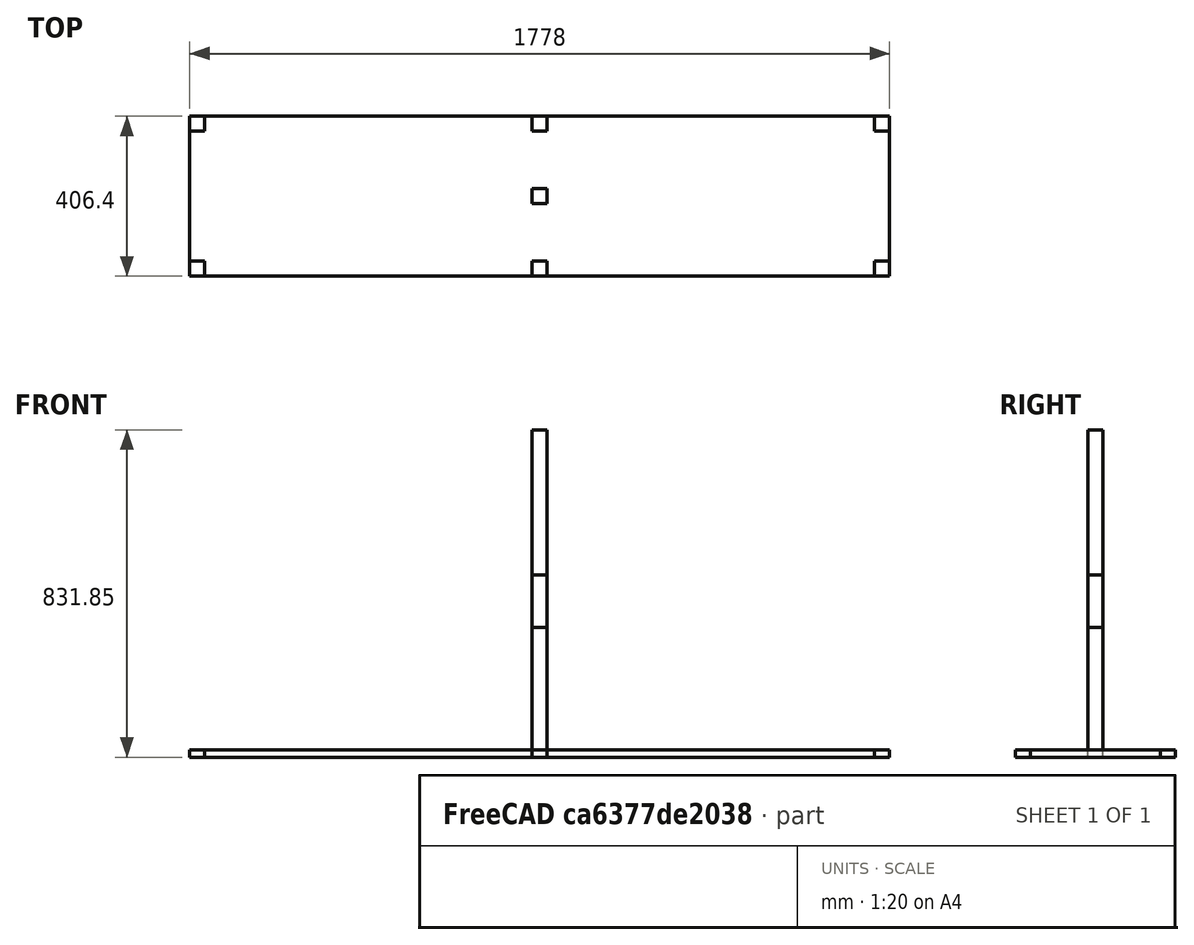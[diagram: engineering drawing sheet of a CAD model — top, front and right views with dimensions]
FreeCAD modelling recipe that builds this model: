
FCSTD DOCUMENT  (FreeCAD 1.1R41155 (Git))
Label: tv_console
License: All rights reserved
LicenseURL: http://en.wikipedia.org/wiki/All_rights_reserved
objects: App::FeaturePython×25, App::Link×22, App::Point×7, Sketcher::SketchObject×5, PartDesign::Pad×5, PartDesign::Body×5, Spreadsheet::Sheet×1, Assembly::JointGroup×1, Assembly::ViewGroup×1, Assembly::BomObject×1, Assembly::BomGroup×1, Assembly::AssemblyObject×1
note: 30 computed .brp shape members not serialized (recipe doc carries the construction recipe); baked Part::Feature solids carry a one-line shape summary decoded from their .brp

FEATURE [Sketcher::SketchObject] Sketch
  ArcFitTolerance = 0
  AttachmentSupport = -> [XY_Plane]
  ExternalTypes = [0]
  FullyConstrained = true
  MakeInternals = false
  MapMode = 5
  sketch-geometry (5):
    g0: LineSegment StartX=-889 StartY=-203.2 StartZ=0 EndX=889 EndY=-203.2 EndZ=0
    g1: LineSegment StartX=889 StartY=-203.2 StartZ=0 EndX=889 EndY=203.2 EndZ=0
    g2: LineSegment StartX=889 StartY=203.2 StartZ=0 EndX=-889 EndY=203.2 EndZ=0
    g3: LineSegment StartX=-889 StartY=203.2 StartZ=0 EndX=-889 EndY=-203.2 EndZ=0
    g4: GeomPoint [constr] X=0 Y=0 Z=0
  constraints (12):
    c: Coincident(g0,g1)
    c: Coincident(g1,g2)
    c: Coincident(g2,g3)
    c: Coincident(g3,g0)
    c: Horizontal(g0)
    c: Horizontal(g2)
    c: Vertical(g1)
    c: Vertical(g3)
    c: Symmetric(g2,g0,g4)
    c: Distance(g1,g3) = 1778
    c: Distance(g0,g2) = 406.4
    c: Coincident(g4,g-1)
FEATURE [PartDesign::Pad] Pad
  Direction = (0,0,1)
  Length = 19.05
  Length2 = 10
  Profile = -> Sketch
  ReferenceAxis = -> Sketch [N_Axis]
  Suppressed = false
  Type = 0
  expr: Length = Spreadsheet.plywood_thickness
FEATURE [PartDesign::Body] Body  label="top"
  AllowCompound = false
  Group = -> [Sketch,Pad]
  Origin = -> Origin
  Tip = -> Pad
FEATURE [Sketcher::SketchObject] Sketch001
  ArcFitTolerance = 0
  AttachmentSupport = -> [XY_Plane001]
  ExternalTypes = [0]
  FullyConstrained = true
  MakeInternals = false
  MapMode = 5
  sketch-geometry (5):
    g0: LineSegment StartX=-19.05 StartY=-19.05 StartZ=0 EndX=19.05 EndY=-19.05 EndZ=0
    g1: LineSegment StartX=19.05 StartY=-19.05 StartZ=0 EndX=19.05 EndY=19.05 EndZ=0
    g2: LineSegment StartX=19.05 StartY=19.05 StartZ=0 EndX=-19.05 EndY=19.05 EndZ=0
    g3: LineSegment StartX=-19.05 StartY=19.05 StartZ=0 EndX=-19.05 EndY=-19.05 EndZ=0
    g4: GeomPoint [constr] X=0 Y=0 Z=0
  constraints (12):
    c: Coincident(g0,g1)
    c: Coincident(g1,g2)
    c: Coincident(g2,g3)
    c: Coincident(g3,g0)
    c: Horizontal(g0)
    c: Horizontal(g2)
    c: Vertical(g1)
    c: Vertical(g3)
    c: Symmetric(g2,g0,g4)
    c: Distance(g1,g3) = 38.1
    c: Distance(g0,g2) = 38.1
    c: Coincident(g4,g-1)
FEATURE [Spreadsheet::Sheet] Spreadsheet
  cells = B3='plywood thickness; C3(plywood_thickness)==0.75 "
FEATURE [PartDesign::Pad] Pad001
  Direction = (0,0,1)
  Length = 463.55
  Length2 = 10
  Profile = -> Sketch001
  ReferenceAxis = -> Sketch001 [N_Axis]
  Suppressed = false
  Type = 0
  expr: Length = 19 " - Spreadsheet.plywood_thickness
FEATURE [PartDesign::Body] Body001  label="leg"
  AllowCompound = false
  Group = -> [Sketch001,Pad001]
  Origin = -> Origin001
  Tip = -> Pad001
FEATURE [Sketcher::SketchObject] Sketch002
  ArcFitTolerance = 0
  AttachmentSupport = -> [XY_Plane002]
  ExternalTypes = [0]
  FullyConstrained = false
  MakeInternals = false
  MapMode = 5
  sketch-geometry (24):
    g0: LineSegment StartX=0 StartY=165.1 StartZ=0 EndX=19.05 EndY=165.1 EndZ=0
    g1: LineSegment StartX=19.05 StartY=165.1 StartZ=0 EndX=19.05 EndY=203.2 EndZ=0
    g2: LineSegment StartX=19.05 StartY=203.2 StartZ=0 EndX=850.9 EndY=203.2 EndZ=0
    g3: LineSegment StartX=850.9 StartY=203.2 StartZ=0 EndX=850.9 EndY=165.1 EndZ=0
    g4: LineSegment StartX=850.9 StartY=165.1 StartZ=0 EndX=889 EndY=165.1 EndZ=0
    g5: LineSegment StartX=889 StartY=165.1 StartZ=0 EndX=889 EndY=0 EndZ=0
    g6: LineSegment StartX=0 StartY=-165.1 StartZ=0 EndX=19.05 EndY=-165.1 EndZ=0
    g7: LineSegment StartX=19.05 StartY=-165.1 StartZ=0 EndX=19.05 EndY=-203.2 EndZ=0
    g8: LineSegment StartX=19.05 StartY=-203.2 StartZ=0 EndX=850.9 EndY=-203.2 EndZ=0
    g9: LineSegment StartX=850.9 StartY=-203.2 StartZ=0 EndX=850.9 EndY=-165.1 EndZ=0
    g10: LineSegment StartX=850.9 StartY=-165.1 StartZ=0 EndX=889 EndY=-165.1 EndZ=0
    g11: LineSegment StartX=889 StartY=-165.1 StartZ=0 EndX=889 EndY=0 EndZ=0
    g12: LineSegment StartX=0 StartY=165.1 StartZ=0 EndX=-19.05 EndY=165.1 EndZ=0
    g13: LineSegment StartX=-19.05 StartY=165.1 StartZ=0 EndX=-19.05 EndY=203.2 EndZ=0
    g14: LineSegment StartX=-19.05 StartY=203.2 StartZ=0 EndX=-850.9 EndY=203.2 EndZ=0
    g15: LineSegment StartX=-850.9 StartY=203.2 StartZ=0 EndX=-850.9 EndY=165.1 EndZ=0
    g16: LineSegment StartX=-850.9 StartY=165.1 StartZ=0 EndX=-889 EndY=165.1 EndZ=0
    g17: LineSegment StartX=-889 StartY=165.1 StartZ=0 EndX=-889 EndY=0 EndZ=0
    g18: LineSegment StartX=0 StartY=-165.1 StartZ=0 EndX=-19.05 EndY=-165.1 EndZ=0
    g19: LineSegment StartX=-19.05 StartY=-165.1 StartZ=0 EndX=-19.05 EndY=-203.2 EndZ=0
    g20: LineSegment StartX=-19.05 StartY=-203.2 StartZ=0 EndX=-850.9 EndY=-203.2 EndZ=0
    g21: LineSegment StartX=-850.9 StartY=-203.2 StartZ=0 EndX=-850.9 EndY=-165.1 EndZ=0
    g22: LineSegment StartX=-850.9 StartY=-165.1 StartZ=0 EndX=-889 EndY=-165.1 EndZ=0
    g23: LineSegment StartX=-889 StartY=-165.1 StartZ=0 EndX=-889 EndY=0 EndZ=0
  constraints (58):
    c: PointOnObject(g0,g-2)
    c: Horizontal(g0)
    c: Coincident(g0,g1)
    c: Vertical(g1)
    c: Coincident(g1,g2)
    c: Horizontal(g2)
    c: Coincident(g2,g3)
    c: Vertical(g3)
    c: Coincident(g3,g4)
    c: Horizontal(g4)
    c: Coincident(g4,g5)
    c: PointOnObject(g5,g-1)
    c: Vertical(g5)
    c: DistanceY(g1,g1) = 38.1
    c: DistanceX(g0,g0) = 19.05
    c: Equal(g3,g1)
    c: DistanceY(g5,g2) = 203.2
    c: DistanceX(g0,g4) = 889
    c: Equal(g4,g3)
    c: Horizontal(g6)
    c: Coincident(g6,g7)
    c: Vertical(g7)
    c: Coincident(g7,g8)
    c: Horizontal(g8)
    c: Coincident(g8,g9)
    c: Vertical(g9)
    c: Coincident(g9,g10)
    c: Horizontal(g10)
    c: Coincident(g10,g11)
    c: Vertical(g11)
    c: Equal(g9,g7)
    c: Equal(g10,g9)
    c: Horizontal(g12)
    c: Coincident(g12,g13)
    c: Vertical(g13)
    c: Coincident(g13,g14)
    c: Horizontal(g14)
    c: Coincident(g14,g15)
    c: Vertical(g15)
    c: Coincident(g15,g16)
    c: Horizontal(g16)
    c: Coincident(g16,g17)
    c: Vertical(g17)
    c: Equal(g15,g13)
    c: Equal(g16,g15)
    c: Horizontal(g18)
    c: Coincident(g18,g19)
    c: Vertical(g19)
    c: Coincident(g19,g20)
    c: Horizontal(g20)
    c: Coincident(g20,g21)
    c: Vertical(g21)
    c: Coincident(g21,g22)
    c: Horizontal(g22)
    c: Coincident(g22,g23)
    c: Vertical(g23)
    c: Equal(g21,g19)
    c: Equal(g22,g21)
FEATURE [PartDesign::Pad] Pad002
  Direction = (0,0,1)
  Length = 19.05
  Length2 = 10
  Profile = -> Sketch002
  ReferenceAxis = -> Sketch002 [N_Axis]
  Suppressed = false
  Type = 0
  expr: Length = Spreadsheet.plywood_thickness
FEATURE [PartDesign::Body] Body002  label="shelf"
  AllowCompound = false
  Group = -> [Sketch002,Pad002]
  Origin = -> Origin002
  Tip = -> Pad002
FEATURE [Sketcher::SketchObject] Sketch003
  ArcFitTolerance = 0
  AttachmentSupport = -> [XY_Plane004]
  ExternalTypes = [0]
  FullyConstrained = true
  MakeInternals = false
  MapMode = 5
  sketch-geometry (5):
    g0: LineSegment StartX=-19.05 StartY=-19.05 StartZ=0 EndX=19.05 EndY=-19.05 EndZ=0
    g1: LineSegment StartX=19.05 StartY=-19.05 StartZ=0 EndX=19.05 EndY=19.05 EndZ=0
    g2: LineSegment StartX=19.05 StartY=19.05 StartZ=0 EndX=-19.05 EndY=19.05 EndZ=0
    g3: LineSegment StartX=-19.05 StartY=19.05 StartZ=0 EndX=-19.05 EndY=-19.05 EndZ=0
    g4: GeomPoint [constr] X=0 Y=0 Z=0
  constraints (12):
    c: Coincident(g0,g1)
    c: Coincident(g1,g2)
    c: Coincident(g2,g3)
    c: Coincident(g3,g0)
    c: Horizontal(g0)
    c: Horizontal(g2)
    c: Vertical(g1)
    c: Vertical(g3)
    c: Symmetric(g2,g0,g4)
    c: Distance(g1,g3) = 38.1
    c: Distance(g0,g2) = 38.1
    c: Coincident(g4,g-1)
FEATURE [PartDesign::Pad] Pad003
  Direction = (0,0,1)
  Length = 831.85
  Length2 = 10
  Profile = -> Sketch003
  ReferenceAxis = -> Sketch003 [N_Axis]
  Suppressed = false
  Type = 0
  expr: Length = 35 " - 2.25 "
FEATURE [PartDesign::Body] Body004  label="long support"
  AllowCompound = false
  Group = -> [Sketch003,Pad003]
  Origin = -> Origin004
  Tip = -> Pad003
FEATURE [Sketcher::SketchObject] Sketch004
  ArcFitTolerance = 0
  AttachmentSupport = -> [XY_Plane005]
  ExternalTypes = [0]
  FullyConstrained = true
  MakeInternals = false
  MapMode = 5
  sketch-geometry (5):
    g0: LineSegment StartX=-19.05 StartY=-19.05 StartZ=0 EndX=19.05 EndY=-19.05 EndZ=0
    g1: LineSegment StartX=19.05 StartY=-19.05 StartZ=0 EndX=19.05 EndY=19.05 EndZ=0
    g2: LineSegment StartX=19.05 StartY=19.05 StartZ=0 EndX=-19.05 EndY=19.05 EndZ=0
    g3: LineSegment StartX=-19.05 StartY=19.05 StartZ=0 EndX=-19.05 EndY=-19.05 EndZ=0
    g4: GeomPoint [constr] X=0 Y=0 Z=0
  constraints (12):
    c: Coincident(g0,g1)
    c: Coincident(g1,g2)
    c: Coincident(g2,g3)
    c: Coincident(g3,g0)
    c: Horizontal(g0)
    c: Horizontal(g2)
    c: Vertical(g1)
    c: Vertical(g3)
    c: Symmetric(g2,g0,g4)
    c: Distance(g1,g3) = 38.1
    c: Distance(g0,g2) = 38.1
    c: Coincident(g4,g-1)
FEATURE [PartDesign::Pad] Pad004
  Direction = (0,0,1)
  Length = 330.2
  Length2 = 10
  Profile = -> Sketch004
  ReferenceAxis = -> Sketch004 [N_Axis]
  Suppressed = false
  Type = 0
  expr: Length = 13 "
FEATURE [PartDesign::Body] Body005  label="short support"
  AllowCompound = false
  Group = -> [Sketch004,Pad004]
  Origin = -> Origin005
  Tip = -> Pad004
FEATURE [App::Point] Origin008  label="Origin"
  Role = Origin
FEATURE [App::Point] Origin009  label="Origin"
  Role = Origin
FEATURE [App::Point] Origin010  label="Origin"
  Role = Origin
FEATURE [App::Point] Origin011  label="Origin"
  Role = Origin
FEATURE [App::Point] Origin012  label="Origin"
  Role = Origin
FEATURE [App::Point] Origin013  label="Origin"
  Role = Origin
FEATURE [App::Point] Origin015
  Role = Origin
FEATURE [App::Link] top
  LinkedObject = -> Body
FEATURE [App::FeaturePython] GroundedJoint  # Assembly grounded joint (typed FeaturePython)
  ObjectToGround = -> top
FEATURE [App::Link] shelf
  LinkPlacement = pos=(0,4.3273e-05,-363) rot=(0,0,1;0rad)
  LinkedObject = -> Body002
  Placement = pos=(0,4.3273e-05,-363) rot=(0,0,1;0rad)
FEATURE [App::Link] leg
  LinkPlacement = pos=(869.95,-184.15,-463.55) rot=(0,0,1;0rad)
  LinkedObject = -> Body001
  Placement = pos=(869.95,-184.15,-463.55) rot=(0,0,1;0rad)
FEATURE [App::Link] leg001
  LinkPlacement = pos=(-869.95,-184.15,-463.55) rot=(0,0,1;0rad)
  LinkedObject = -> Body001
  Placement = pos=(-869.95,-184.15,-463.55) rot=(0,0,1;0rad)
FEATURE [App::Link] leg002
  LinkPlacement = pos=(-869.95,184.15,-463.55) rot=(0,0,1;0rad)
  LinkedObject = -> Body001
  Placement = pos=(-869.95,184.15,-463.55) rot=(0,0,1;0rad)
FEATURE [App::Link] leg003
  LinkPlacement = pos=(-2.076e-13,-184.15,-463.55) rot=(0,0,1;0rad)
  LinkedObject = -> Body001
  Placement = pos=(-2.076e-13,-184.15,-463.55) rot=(0,0,1;0rad)
FEATURE [App::Link] leg004
  LinkPlacement = pos=(2.052e-13,184.15,-463.55) rot=(0,0,1;0rad)
  LinkedObject = -> Body001
  Placement = pos=(2.052e-13,184.15,-463.55) rot=(0,0,1;0rad)
FEATURE [App::Link] leg005
  LinkPlacement = pos=(869.95,184.15,-463.55) rot=(0,0,1;0rad)
  LinkedObject = -> Body001
  Placement = pos=(869.95,184.15,-463.55) rot=(0,0,1;0rad)
FEATURE [App::Link] short_support  label="short support001"
  LinkPlacement = pos=(869.95,165.1,-19.05) rot=(1,0,0;1.5708rad)
  LinkedObject = -> Body005
  Placement = pos=(869.95,165.1,-19.05) rot=(1,0,0;1.5708rad)
FEATURE [App::Link] short_support001  label="short support002"
  LinkPlacement = pos=(-869.95,165.1,-19.05) rot=(1,0,0;1.5708rad)
  LinkedObject = -> Body005
  Placement = pos=(-869.95,165.1,-19.05) rot=(1,0,0;1.5708rad)
FEATURE [App::Link] short_support002  label="short support003"
  LinkPlacement = pos=(1.02e-14,165.1,-19.05) rot=(1,0,0;1.5708rad)
  LinkedObject = -> Body005
  Placement = pos=(1.02e-14,165.1,-19.05) rot=(1,0,0;1.5708rad)
FEATURE [App::Link] short_support003  label="short support004"
  LinkPlacement = pos=(0,165.1,-382.05) rot=(1,0,0;1.5708rad)
  LinkedObject = -> Body005
  Placement = pos=(0,165.1,-382.05) rot=(1,0,0;1.5708rad)
FEATURE [App::Link] short_support004  label="short support005"
  LinkPlacement = pos=(869.95,165.1,-382.05) rot=(1,0,0;1.5708rad)
  LinkedObject = -> Body005
  Placement = pos=(869.95,165.1,-382.05) rot=(1,0,0;1.5708rad)
FEATURE [App::Link] short_support005  label="short support006"
  LinkPlacement = pos=(-869.95,165.1,-382.05) rot=(1,0,0;1.5708rad)
  LinkedObject = -> Body005
  Placement = pos=(-869.95,165.1,-382.05) rot=(1,0,0;1.5708rad)
FEATURE [App::Link] long_support  label="long support001"
  LinkPlacement = pos=(19.05,184.15,-19.05) rot=(0,1,0;1.5708rad)
  LinkedObject = -> Body004
  Placement = pos=(19.05,184.15,-19.05) rot=(0,1,0;1.5708rad)
FEATURE [App::Link] long_support001  label="long support002"
  LinkPlacement = pos=(-850.9,184.15,-19.05) rot=(0,1,0;1.5708rad)
  LinkedObject = -> Body004
  Placement = pos=(-850.9,184.15,-19.05) rot=(0,1,0;1.5708rad)
FEATURE [App::Link] long_support002  label="long support003"
  LinkPlacement = pos=(19.05,-184.15,-19.05) rot=(0,1,0;1.5708rad)
  LinkedObject = -> Body004
  Placement = pos=(19.05,-184.15,-19.05) rot=(0,1,0;1.5708rad)
FEATURE [App::Link] long_support003  label="long support004"
  LinkPlacement = pos=(-850.9,-184.15,-19.05) rot=(0,1,0;1.5708rad)
  LinkedObject = -> Body004
  Placement = pos=(-850.9,-184.15,-19.05) rot=(0,1,0;1.5708rad)
FEATURE [App::Link] long_support004  label="long support005"
  LinkPlacement = pos=(-19.05,-184.15,-382.05) rot=(0,1,0;4.71239rad)
  LinkedObject = -> Body004
  Placement = pos=(-19.05,-184.15,-382.05) rot=(0,1,0;4.71239rad)
FEATURE [App::Link] long_support005  label="long support006"
  LinkPlacement = pos=(-19.05,184.15,-382.05) rot=(0,-1,0;1.5708rad)
  LinkedObject = -> Body004
  Placement = pos=(-19.05,184.15,-382.05) rot=(0,-1,0;1.5708rad)
FEATURE [App::Link] long_support006  label="long support007"
  LinkPlacement = pos=(850.9,-184.15,-382.05) rot=(0,-1,0;1.5708rad)
  LinkedObject = -> Body004
  Placement = pos=(850.9,-184.15,-382.05) rot=(0,-1,0;1.5708rad)
FEATURE [App::Link] long_support007  label="long support008"
  LinkPlacement = pos=(850.9,184.15,-382.05) rot=(0,-1,0;1.5708rad)
  LinkedObject = -> Body004
  Placement = pos=(850.9,184.15,-382.05) rot=(0,-1,0;1.5708rad)
FEATURE [App::FeaturePython] Joint  label="Fixed016"  # Assembly joint (typed FeaturePython)
  Activated = true
  AngleMax = 0
  AngleMin = 0
  Detach1 = false
  Detach2 = false
  Distance = 0
  Distance2 = 0
  EnableAngleMax = false
  EnableAngleMin = false
  EnableLengthMax = false
  EnableLengthMin = false
  JointType = 0 (Fixed)
  LengthMax = 0
  LengthMin = 0
  Placement1 = pos=(19.05,-19.05,463.55) rot=(0,0,1;0rad)
  Placement2 = pos=(889,-203.2,0) rot=(0,0,1;0rad)
  Reference1 = -> Assembly [leg.Vertex4,leg.Vertex4]
  Reference2 = -> Assembly [top.Vertex3,top.Vertex3]
FEATURE [App::FeaturePython] Joint001  label="Fixed017"  # Assembly joint (typed FeaturePython)
  Activated = true
  AngleMax = 0
  AngleMin = 0
  Detach1 = false
  Detach2 = false
  Distance = 0
  Distance2 = 0
  EnableAngleMax = false
  EnableAngleMin = false
  EnableLengthMax = false
  EnableLengthMin = false
  JointType = 0 (Fixed)
  LengthMax = 0
  LengthMin = 0
  Placement1 = pos=(0,-203.2,0) rot=(0.707107,0,0.707107;3.14159rad)
  Placement2 = pos=(1.7e-15,-19.05,463.55) rot=(0.707107,0,0.707107;3.14159rad)
  Reference1 = -> Assembly [top.Edge3,top.Edge3]
  Reference2 = -> Assembly [leg003.Edge4,leg003.Edge4]
FEATURE [App::FeaturePython] Joint002  label="Fixed018"  # Assembly joint (typed FeaturePython)
  Activated = true
  AngleMax = 0
  AngleMin = 0
  Detach1 = false
  Detach2 = false
  Distance = 0
  Distance2 = 0
  EnableAngleMax = false
  EnableAngleMin = false
  EnableLengthMax = false
  EnableLengthMin = false
  JointType = 0 (Fixed)
  LengthMax = 0
  LengthMin = 0
  Placement1 = pos=(-889,-203.2,0) rot=(0,0,1;0rad)
  Placement2 = pos=(-19.05,-19.05,463.55) rot=(0,0,1;0rad)
  Reference1 = -> Assembly [top.Vertex1,top.Vertex1]
  Reference2 = -> Assembly [leg001.Vertex2,leg001.Vertex2]
FEATURE [App::FeaturePython] Joint003  label="Fixed019"  # Assembly joint (typed FeaturePython)
  Activated = true
  AngleMax = 0
  AngleMin = 0
  Detach1 = false
  Detach2 = false
  Distance = 0
  Distance2 = 0
  EnableAngleMax = false
  EnableAngleMin = false
  EnableLengthMax = false
  EnableLengthMin = false
  JointType = 0 (Fixed)
  LengthMax = 0
  LengthMin = 0
  Placement1 = pos=(-19.05,19.05,463.55) rot=(0,0,1;0rad)
  Placement2 = pos=(-889,203.2,0) rot=(0,0,1;0rad)
  Reference1 = -> Assembly [leg002.Vertex8,leg002.Vertex8]
  Reference2 = -> Assembly [top.Vertex7,top.Vertex7]
FEATURE [App::FeaturePython] Joint004  label="Fixed020"  # Assembly joint (typed FeaturePython)
  Activated = true
  AngleMax = 0
  AngleMin = 0
  Detach1 = false
  Detach2 = false
  Distance = 0
  Distance2 = 0
  EnableAngleMax = false
  EnableAngleMin = false
  EnableLengthMax = false
  EnableLengthMin = false
  JointType = 0 (Fixed)
  LengthMax = 0
  LengthMin = 0
  Placement1 = pos=(0,203.2,0) rot=(-0.707107,0,0.707107;3.14159rad)
  Placement2 = pos=(7e-16,19.05,463.55) rot=(-0.707107,0,0.707107;3.14159rad)
  Reference1 = -> Assembly [top.Edge9,top.Edge9]
  Reference2 = -> Assembly [leg004.Edge10,leg004.Edge10]
FEATURE [App::FeaturePython] Joint005  label="Fixed021"  # Assembly joint (typed FeaturePython)
  Activated = true
  AngleMax = 0
  AngleMin = 0
  Detach1 = false
  Detach2 = false
  Distance = 0
  Distance2 = 0
  EnableAngleMax = false
  EnableAngleMin = false
  EnableLengthMax = false
  EnableLengthMin = false
  JointType = 0 (Fixed)
  LengthMax = 0
  LengthMin = 0
  Placement1 = pos=(889,203.2,0) rot=(0,0,1;0rad)
  Placement2 = pos=(19.05,19.05,463.55) rot=(0,0,1;0rad)
  Reference1 = -> Assembly [top.Vertex5,top.Vertex5]
  Reference2 = -> Assembly [leg005.Vertex6,leg005.Vertex6]
FEATURE [App::FeaturePython] Joint006  label="Fixed025"  # Assembly joint (typed FeaturePython)
  Activated = true
  AngleMax = 0
  AngleMin = 0
  Detach1 = false
  Detach2 = false
  Distance = 0
  Distance2 = 0
  EnableAngleMax = false
  EnableAngleMin = false
  EnableLengthMax = false
  EnableLengthMin = false
  JointType = 0 (Fixed)
  LengthMax = 0
  LengthMin = 0
  Offset2 = pos=(0,0,0) rot=(0,0,-1;1.5708rad)
  Placement1 = pos=(-19.05,0,0) rot=(-0.57735,-0.57735,0.57735;4.18879rad)
  Placement2 = pos=(19.05,0,463.55) rot=(0,0.707107,0.707107;3.14159rad)
  Reference1 = -> Assembly [long_support001.Edge11,long_support001.Edge11]
  Reference2 = -> Assembly [leg002.Edge7,leg002.Edge7]
FEATURE [App::FeaturePython] Joint007  label="Fixed026"  # Assembly joint (typed FeaturePython)
  Activated = true
  AngleMax = 0
  AngleMin = 0
  Detach1 = false
  Detach2 = false
  Distance = 0
  Distance2 = 0
  EnableAngleMax = false
  EnableAngleMin = false
  EnableLengthMax = false
  EnableLengthMin = false
  JointType = 0 (Fixed)
  LengthMax = 0
  LengthMin = 0
  Offset2 = pos=(0,0,0) rot=(0,0,-1;1.5708rad)
  Placement1 = pos=(-19.05,0,0) rot=(-0.57735,-0.57735,0.57735;4.18879rad)
  Placement2 = pos=(19.05,0,463.55) rot=(0,0.707107,0.707107;3.14159rad)
  Reference1 = -> Assembly [long_support.Edge11,long_support.Edge11]
  Reference2 = -> Assembly [leg004.Edge7,leg004.Edge7]
FEATURE [App::FeaturePython] Joint008  label="Fixed027"  # Assembly joint (typed FeaturePython)
  Activated = true
  AngleMax = 0
  AngleMin = 0
  Detach1 = false
  Detach2 = false
  Distance = 0
  Distance2 = 0
  EnableAngleMax = false
  EnableAngleMin = false
  EnableLengthMax = false
  EnableLengthMin = false
  JointType = 0 (Fixed)
  LengthMax = 0
  LengthMin = 0
  Offset2 = pos=(0,0,0) rot=(0,0,-1;1.5708rad)
  Placement1 = pos=(-19.05,0,831.85) rot=(-0.57735,-0.57735,0.57735;4.18879rad)
  Placement2 = pos=(-19.05,0,463.55) rot=(0,-0.707107,0.707107;3.14159rad)
  Reference1 = -> Assembly [long_support003.Edge12,long_support003.Edge12]
  Reference2 = -> Assembly [leg003.Edge12,leg003.Edge12]
FEATURE [App::FeaturePython] Joint009  label="Fixed028"  # Assembly joint (typed FeaturePython)
  Activated = true
  AngleMax = 0
  AngleMin = 0
  Detach1 = false
  Detach2 = false
  Distance = 0
  Distance2 = 0
  EnableAngleMax = false
  EnableAngleMin = false
  EnableLengthMax = false
  EnableLengthMin = false
  JointType = 0 (Fixed)
  LengthMax = 0
  LengthMin = 0
  Offset2 = pos=(0,0,0) rot=(0,0,1;1.5708rad)
  Placement1 = pos=(-19.05,0,463.55) rot=(-0.57735,-0.57735,0.57735;4.18879rad)
  Placement2 = pos=(-19.05,0,831.85) rot=(-1,0,0;4.71239rad)
  Reference1 = -> Assembly [leg.Edge12,leg.Edge12]
  Reference2 = -> Assembly [long_support002.Edge12,long_support002.Edge12]
FEATURE [App::FeaturePython] Joint010  label="Fixed029"  # Assembly joint (typed FeaturePython)
  Activated = true
  AngleMax = 0
  AngleMin = 0
  Detach1 = false
  Detach2 = false
  Distance = 0
  Distance2 = 0
  EnableAngleMax = false
  EnableAngleMin = false
  EnableLengthMax = false
  EnableLengthMin = false
  JointType = 0 (Fixed)
  LengthMax = 0
  LengthMin = 0
  Offset2 = pos=(0,0,0) rot=(0,0,-1;1.5708rad)
  Placement1 = pos=(0,19.05,0) rot=(-0.707107,0,0.707107;3.14159rad)
  Placement2 = pos=(0,-19.05,463.55) rot=(0.57735,0.57735,0.57735;2.0944rad)
  Reference1 = -> Assembly [short_support.Edge9,short_support.Edge9]
  Reference2 = -> Assembly [leg005.Edge4,leg005.Edge4]
FEATURE [App::FeaturePython] Joint011  label="Fixed030"  # Assembly joint (typed FeaturePython)
  Activated = true
  AngleMax = 0
  AngleMin = 0
  Detach1 = false
  Detach2 = false
  Distance = 0
  Distance2 = 0
  EnableAngleMax = false
  EnableAngleMin = false
  EnableLengthMax = false
  EnableLengthMin = false
  JointType = 0 (Fixed)
  LengthMax = 0
  LengthMin = 0
  Offset2 = pos=(0,0,0) rot=(0,0,-1;1.5708rad)
  Placement1 = pos=(0,19.05,0) rot=(-0.707107,0,0.707107;3.14159rad)
  Placement2 = pos=(0,-19.05,463.55) rot=(0.57735,0.57735,0.57735;2.0944rad)
  Reference1 = -> Assembly [short_support001.Edge9,short_support001.Edge9]
  Reference2 = -> Assembly [leg002.Edge4,leg002.Edge4]
FEATURE [App::FeaturePython] Joint012  label="Fixed031"  # Assembly joint (typed FeaturePython)
  Activated = true
  AngleMax = 0
  AngleMin = 0
  Detach1 = false
  Detach2 = false
  Distance = 0
  Distance2 = 0
  EnableAngleMax = false
  EnableAngleMin = false
  EnableLengthMax = false
  EnableLengthMin = false
  JointType = 0 (Fixed)
  LengthMax = 0
  LengthMin = 0
  Offset2 = pos=(0,0,0) rot=(0,0,-1;1.5708rad)
  Placement1 = pos=(-1.7e-15,19.05,0) rot=(-0.707107,0,0.707107;3.14159rad)
  Placement2 = pos=(7e-16,-19.05,463.55) rot=(0.57735,0.57735,0.57735;2.0944rad)
  Reference1 = -> Assembly [short_support002.Edge9,short_support002.Edge9]
  Reference2 = -> Assembly [leg004.Edge4,leg004.Edge4]
FEATURE [App::FeaturePython] Joint013  label="Fixed032"  # Assembly joint (typed FeaturePython)
  Activated = true
  AngleMax = 0
  AngleMin = 0
  Detach1 = false
  Detach2 = false
  Distance = 0
  Distance2 = 0
  EnableAngleMax = false
  EnableAngleMin = false
  EnableLengthMax = false
  EnableLengthMin = false
  JointType = 0 (Fixed)
  LengthMax = 0
  LengthMin = 0
  Offset2 = pos=(0,0,0) rot=(0,0,-1;1.5708rad)
  Placement1 = pos=(0,19.05,0) rot=(-0.707107,0,0.707107;3.14159rad)
  Placement2 = pos=(-869.95,165.1,0) rot=(-0.57735,-0.57735,0.57735;2.0944rad)
  Reference1 = -> Assembly [short_support005.Edge9,short_support005.Edge9]
  Reference2 = -> Assembly [shelf.Edge60,shelf.Edge60]
FEATURE [App::FeaturePython] Joint014  label="Fixed034"  # Assembly joint (typed FeaturePython)
  Activated = true
  AngleMax = 0
  AngleMin = 0
  Detach1 = false
  Detach2 = false
  Distance = 0
  Distance2 = 0
  EnableAngleMax = false
  EnableAngleMin = false
  EnableLengthMax = false
  EnableLengthMin = false
  JointType = 0 (Fixed)
  LengthMax = 0
  LengthMin = 0
  Offset2 = pos=(0,0,0) rot=(0,0,-1;1.5708rad)
  Placement1 = pos=(0,19.05,0) rot=(-0.707107,0,0.707107;3.14159rad)
  Placement2 = pos=(0,165.1,0) rot=(-0.57735,-0.57735,0.57735;2.0944rad)
  Reference1 = -> Assembly [short_support003.Edge9,short_support003.Edge9]
  Reference2 = -> Assembly [shelf.Edge71,shelf.Vertex1]
FEATURE [App::FeaturePython] Joint015  label="Fixed035"  # Assembly joint (typed FeaturePython)
  Activated = true
  AngleMax = 0
  AngleMin = 0
  Detach1 = false
  Detach2 = false
  Distance = 0
  Distance2 = 0
  EnableAngleMax = false
  EnableAngleMin = false
  EnableLengthMax = false
  EnableLengthMin = false
  JointType = 0 (Fixed)
  LengthMax = 0
  LengthMin = 0
  Offset2 = pos=(0,0,0) rot=(0,0,-1;1.5708rad)
  Placement1 = pos=(0,19.05,0) rot=(-0.707107,0,0.707107;3.14159rad)
  Placement2 = pos=(869.95,165.1,0) rot=(0.57735,0.57735,0.57735;2.0944rad)
  Reference1 = -> Assembly [short_support004.Edge9,short_support004.Edge9]
  Reference2 = -> Assembly [shelf.Edge15,shelf.Edge15]
FEATURE [App::FeaturePython] Joint016  label="Fixed036"  # Assembly joint (typed FeaturePython)
  Activated = true
  AngleMax = 0
  AngleMin = 0
  Detach1 = false
  Detach2 = false
  Distance = 0
  Distance2 = 0
  EnableAngleMax = false
  EnableAngleMin = false
  EnableLengthMax = false
  EnableLengthMin = false
  JointType = 0 (Fixed)
  LengthMax = 0
  LengthMin = 0
  Offset2 = pos=(0,0,0) rot=(0,0,-1;1.5708rad)
  Placement1 = pos=(19.05,0,0) rot=(0.57735,0.57735,0.57735;4.18879rad)
  Placement2 = pos=(850.9,-184.15,0) rot=(0,0.707107,0.707107;3.14159rad)
  Reference1 = -> Assembly [long_support006.Edge6,long_support006.Edge6]
  Reference2 = -> Assembly [shelf.Edge27,shelf.Edge27]
FEATURE [App::FeaturePython] Joint017  label="Fixed040"  # Assembly joint (typed FeaturePython)
  Activated = true
  AngleMax = 0
  AngleMin = 0
  Detach1 = false
  Detach2 = false
  Distance = 0
  Distance2 = 0
  EnableAngleMax = false
  EnableAngleMin = false
  EnableLengthMax = false
  EnableLengthMin = false
  JointType = 0 (Fixed)
  LengthMax = 0
  LengthMin = 0
  Offset2 = pos=(0,0,0) rot=(0,0,1;3.14159rad)
  Placement1 = pos=(19.05,-19.05,0) rot=(0,0,1;0rad)
  Placement2 = pos=(-19.05,19.05,0) rot=(0.57735,0.57735,0.57735;2.0944rad)
  Reference1 = -> Assembly [long_support007.Edge2,long_support007.Vertex3]
  Reference2 = -> Assembly [short_support004.Face4,short_support004.Vertex7]
FEATURE [App::FeaturePython] Joint018  label="Fixed041"  # Assembly joint (typed FeaturePython)
  Activated = true
  AngleMax = 0
  AngleMin = 0
  Detach1 = false
  Detach2 = false
  Distance = 0
  Distance2 = 0
  EnableAngleMax = false
  EnableAngleMin = false
  EnableLengthMax = false
  EnableLengthMin = false
  JointType = 0 (Fixed)
  LengthMax = 0
  LengthMin = 0
  Offset2 = pos=(0,0,0) rot=(0,0,1;3.14159rad)
  Placement1 = pos=(19.05,-19.05,0) rot=(0,0,1;0rad)
  Placement2 = pos=(-19.05,-203.2,0) rot=(0,1,0;4.71239rad)
  Reference1 = -> Assembly [long_support004.Edge2,long_support004.Vertex3]
  Reference2 = -> Assembly [shelf.Edge45,shelf.Vertex29]
FEATURE [App::FeaturePython] Joint019  label="Fixed042"  # Assembly joint (typed FeaturePython)
  Activated = true
  AngleMax = 0
  AngleMin = 0
  Detach1 = false
  Detach2 = false
  Distance = 0
  Distance2 = 0
  EnableAngleMax = false
  EnableAngleMin = false
  EnableLengthMax = false
  EnableLengthMin = false
  JointType = 0 (Fixed)
  LengthMax = 0
  LengthMin = 0
  Offset2 = pos=(0,0,0) rot=(0,0,1;3.14159rad)
  Placement1 = pos=(19.05,-19.05,3.6e-15) rot=(0,0,1;0rad)
  Placement2 = pos=(-19.05,19.05,0) rot=(0.57735,0.57735,0.57735;2.0944rad)
  Reference1 = -> Assembly [long_support005.Edge2,long_support005.Vertex3]
  Reference2 = -> Assembly [short_support003.Face4,short_support003.Vertex7]
FEATURE [Assembly::JointGroup] Joints
  Group = -> [GroundedJoint,Joint,Joint001,Joint002,Joint003,Joint004,Joint005,Joint006,Joint007,Joint008,Joint009,Joint010,Joint011,Joint012,Joint013,Joint014,Joint015,Joint016,Joint017,Joint018,Joint019]
FEATURE [App::FeaturePython] Move  # WARN: FeaturePython — macro-defined, semantics opaque (R4)
  MoveType = 1
  MovementTransform = pos=(0,-3e-05,215) rot=(0,0,1;0rad)
  References = -> Assembly [top.,shelf.,leg.,leg001.,leg002.,leg003.,leg004.,leg005.,short_support.,short_support001.,short_support002.,short_support003.,short_support004.,short_support005.,long_support.,long_support001.,long_support002.,long_support003.,long_support004.,long_support005.,long_support006.,long_support007.]
FEATURE [App::FeaturePython] Move001  # WARN: FeaturePython — macro-defined, semantics opaque (R4)
  MoveType = 0
  MovementTransform = pos=(0,-2e-05,175) rot=(0,0,1;0rad)
  References = -> Assembly [top.]
FEATURE [App::FeaturePython] Move002  # WARN: FeaturePython — macro-defined, semantics opaque (R4)
  MoveType = 0
  MovementTransform = pos=(0,-3e-05,216) rot=(0,0,1;0rad)
  References = -> Assembly [shelf.]
FEATURE [App::FeaturePython] Exploded_View  # WARN: FeaturePython — macro-defined, semantics opaque (R4)
  Group = -> [Move,Move001,Move002]
FEATURE [Assembly::ViewGroup] Exploded_Views
  Group = -> [Exploded_View]
FEATURE [Assembly::BomObject] Bill_of_Materials
  cells = A1='Index; B1='Name; C1='Description; D1='Quantity; A2='1; B2='top; C2='3/4 inch plywood 16"x70"; D2=1; A3='2; B3='shelf; C3='3/4 inch plywood 16"x70" with 1.5" cutouts; D3=1; A4='3; B4='leg; C4='2x2 (1.5"x1.5") 18.25"; D4=6; A5='4; B5='short support; C5='2x2 (1.5"x1.5") 13"; D5=6; A6='5; B6='long support; C6='2x2 (1.5"x1.5") 32.75"; D6=8
  columnsNames = Index | Name | Description | Quantity
  detailParts = true
  detailSubAssemblies = true
  onlyParts = false
FEATURE [Assembly::BomGroup] Bills_of_Materials
  Group = -> [Bill_of_Materials]
FEATURE [Assembly::AssemblyObject] Assembly
  Group = -> [Joints,top,GroundedJoint,shelf,leg,leg001,leg002,leg003,leg004,leg005,short_support,short_support001,short_support002,short_support003,short_support004,short_support005,long_support,long_support001,long_support002,long_support003,long_support004,long_support005,long_support006,long_support007,Joint,Joint001,Joint002,Joint003,Joint004,Joint005,Joint006,Joint007,Joint008,Joint009,Joint010,Joint011,+15 more]
  Origin = -> Origin014
  Type = Assembly
